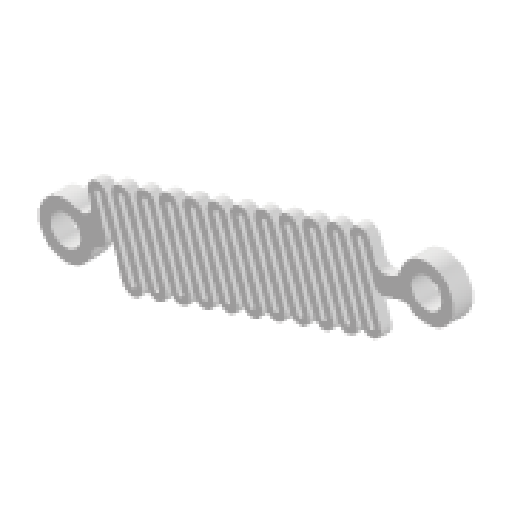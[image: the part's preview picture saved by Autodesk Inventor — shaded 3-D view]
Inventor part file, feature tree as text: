
AUTODESK INVENTOR PART (.ipt)
format: ipt  version: 2025.1 (Build 291241020, 241B)  size: 391,168 bytes
history: native  units: in
note: dims shown in document units (in); Inventor stores cm internally (conversion verified against a paired STEP export)
features: sketch x3, extrude x2, fillet x2
ambient origin geometry x8: Origin, YZ Plane, XZ Plane, XY Plane, X Axis, Y Axis, Z Axis, Center Point
bodies: Solid1 (feature_tree)
feature tree (7):
  extrude  "Extrusion1"  Depth=0.3in
  fillet  "Fillet1"  Radius=0.165in
  fillet  "Fillet2"  Radius=0.3in
  extrude  "Extrusion2"  Depth=0.7in
  sketch  "Sketch1"  dims[d0=0.165in d1=0.3in d2=0.165in d3=0.3in]
  sketch  "Sketch Rectangular Pattern1"  dims[d4=2.0in d5=0.7in]
  sketch  "Sketch2"  dims[d6=0.1in d7=0.05in d8=0.5in d9=0.25in d10=0.03in d11=0.04in d12=0.04in d13=0.03in d14=0.04in d15=0.04in d16=0.2in d17=4.7244in d19=0.14in d20=0.3937in d22=1.0in d25=0.06in d26=0.0in d27=0.015in d28=0.055in d29=0.05in d30=0.0in d31=0.11in d32=0.0in d33=0.03in d34=0.03in]
